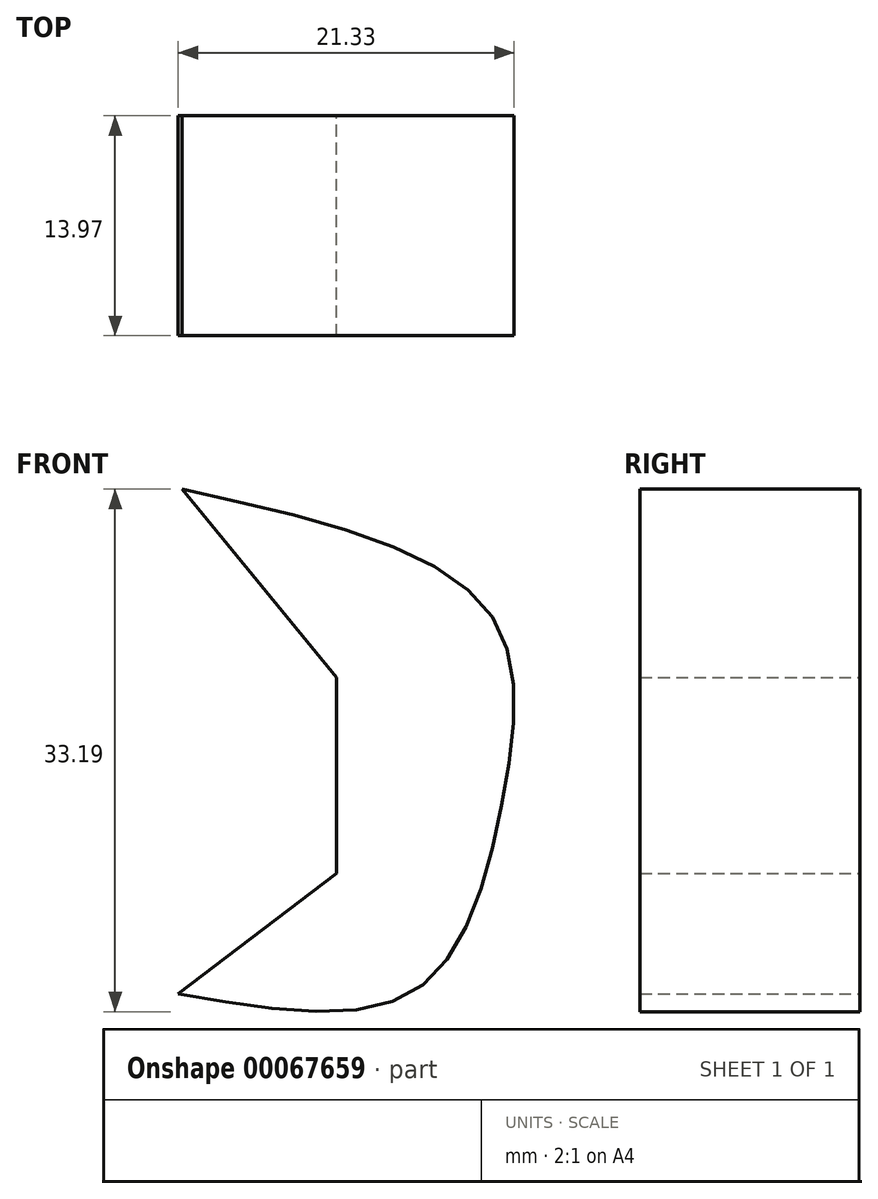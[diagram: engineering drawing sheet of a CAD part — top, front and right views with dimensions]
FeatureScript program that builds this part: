
annotation { "Feature Type Name" : "Feature", "Feature Type Description" : "" }
export const myFeature = defineFeature(function(context is Context, id is Id, definition is map)
    precondition{}
    {
        {
            var Q0;
            Q0=qCreatedBy(makeId("Top.planeOp"),FACE);
            var sketch = newSketch(context, id + "F0", { "sketchPlane" : qUnion([Q0])});
            skCircle(sketch, "E0", {"center": v(0, 0) * mm, "radius": 32.4 * mm});
            skSolve(sketch);
        }
        {
            var Q0;
            Q0=sQuery(id+"F0.wireOp",EDGE,"E0");
            extrude(context, id + "F1", {"bodyType" : ToolBodyType.SURFACE, "surfaceEntities" : qUnion([Q0]), "depth" : 63.5 * mm});
        }
        {
            var Q0;
            Q0=qCreatedBy(makeId("Front.planeOp"),FACE);
            var sketch = newSketch(context, id + "F2", { "sketchPlane" : qUnion([Q0])});
            skLineSegment(sketch, "E1", {"start": v(30.14, 53.7) * mm, "end": v(39.95, 41.74) * mm});
            skLineSegment(sketch, "E2", {"start": v(39.95, 41.74) * mm, "end": v(39.95, 29.3) * mm});
            skLineSegment(sketch, "E3", {"start": v(39.95, 29.3) * mm, "end": v(29.9, 21.65) * mm});
            skFitSpline(sketch, "E4", {"points": [v(30.14, 53.7) * mm, v(49.51, 46.04) * mm, v(50.47, 33.85) * mm, v(44.97, 21.89) * mm, v(29.9, 21.65) * mm], "startDerivative": vector(83.17, -18.38) * mm, "endDerivative": vector(-69.55, 12.29) * mm});
            skSolve(sketch);
        }
        {
            var Q0;
            Q0 = qSketchRegion(id + "F2", true);
            extrude(context, id + "F3", {"entities" : qUnion([Q0]), "depth" : 13.97 * mm});
        }
    });
